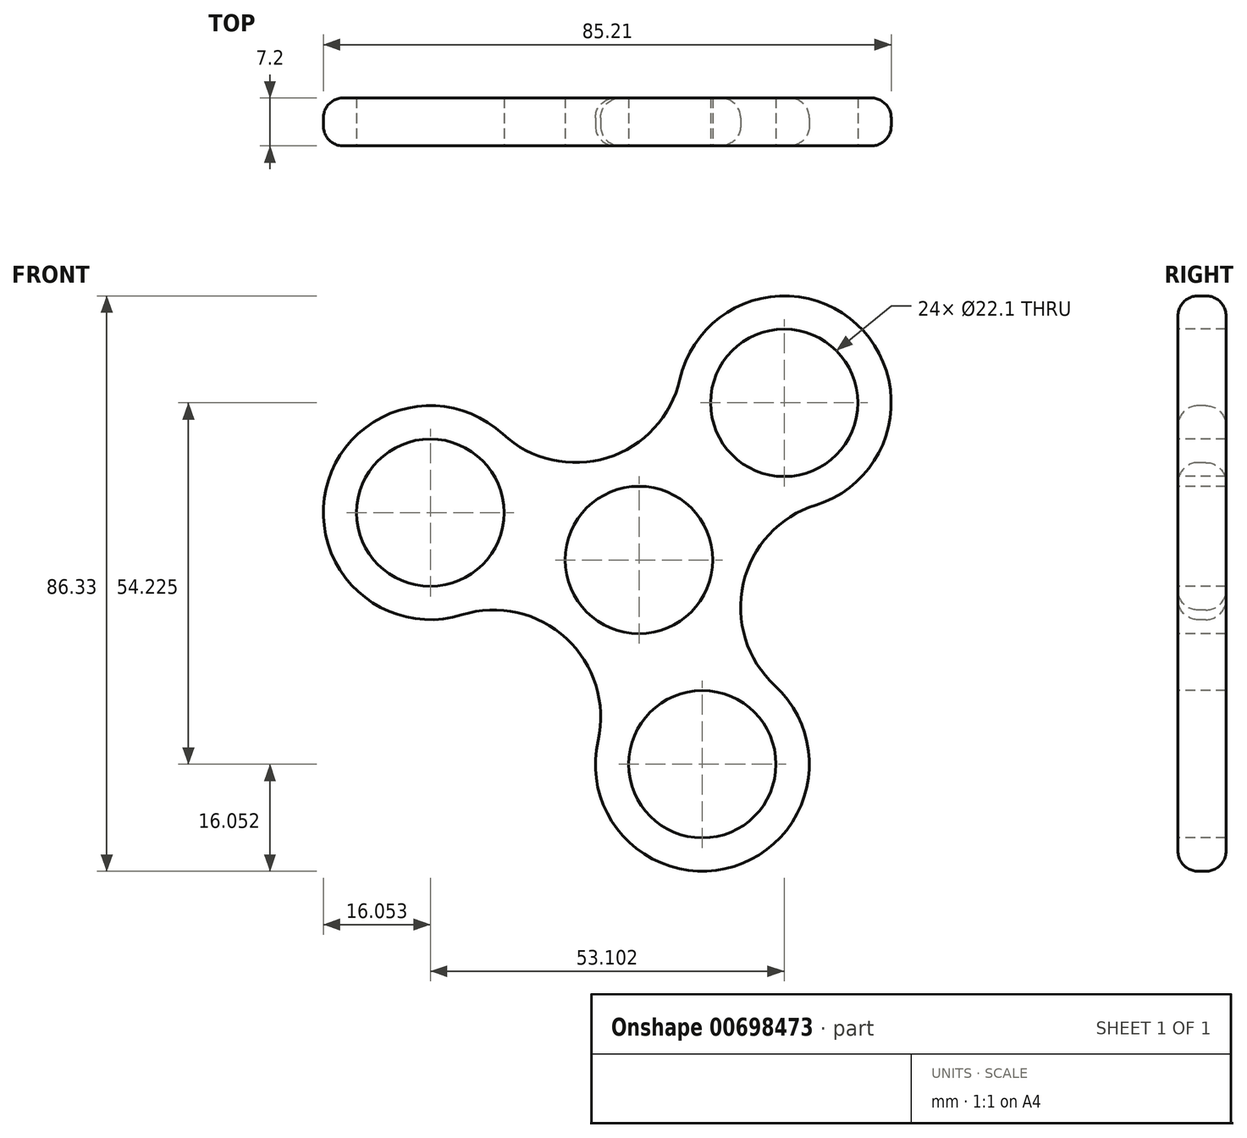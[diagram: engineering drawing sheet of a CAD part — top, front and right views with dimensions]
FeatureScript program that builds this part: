
annotation { "Feature Type Name" : "Feature", "Feature Type Description" : "" }
export const myFeature = defineFeature(function(context is Context, id is Id, definition is map)
    precondition{}
    {
        {
            var Q0;
            Q0=qCreatedBy(makeId("Front.planeOp"),FACE);
            var sketch = newSketch(context, id + "F0", { "sketchPlane" : qUnion([Q0])});
            skCircle(sketch, "E0", {"center": v(0, 0) * mm, "radius": 11.05 * mm});
            skCircle(sketch, "E1", {"center": v(-31.3, 7.1) * mm, "radius": 11.05 * mm});
            skCircle(sketch, "E2", {"center": v(21.8, 23.57) * mm, "radius": 11.05 * mm});
            skCircle(sketch, "E3", {"center": v(9.51, -30.66) * mm, "radius": 11.05 * mm});
            skLineSegment(sketch, "E4", {"start": v(21.8, 23.57) * mm, "end": v(0, 0) * mm});
            skLineSegment(sketch, "E5", {"start": v(0, 0) * mm, "end": v(-31.3, 7.1) * mm});
            skLineSegment(sketch, "E6", {"start": v(0, 0) * mm, "end": v(9.51, -30.66) * mm});
            skLineSegment(sketch, "E7", {"start": v(21.8, 23.57) * mm, "end": v(-31.3, 7.1) * mm, "construction": true});
            skLineSegment(sketch, "E8", {"start": v(-31.3, 7.1) * mm, "end": v(9.51, -30.66) * mm, "construction": true});
            skLineSegment(sketch, "E9", {"start": v(9.51, -30.66) * mm, "end": v(21.8, 23.57) * mm, "construction": true});
            skCircle(sketch, "E10.0", {"center": v(-31.3, 7.1) * mm, "radius": 16.05 * mm});
            skCircle(sketch, "E11.0", {"center": v(21.8, 23.57) * mm, "radius": 16.05 * mm});
            skCircle(sketch, "E12.0", {"center": v(9.51, -30.66) * mm, "radius": 16.05 * mm});
            skCircle(sketch, "E13.0", {"center": v(0, 0) * mm, "radius": 16.05 * mm});
            skLineSegment(sketch, "E14", {"start": v(0, 0) * mm, "end": v(-26.55, -8.24) * mm, "construction": true});
            skLineSegment(sketch, "E15", {"start": v(0, 0) * mm, "end": v(-6.14, -27.11) * mm, "construction": true});
            skArc(sketch, "E16", {"start": v(-6.14, -27.11) * mm, "mid": v(-10.9, -11.78) * mm, "end": v(-26.55, -8.24) * mm});
            skArc(sketch, "E17.1.0", {"start": v(26.55, 8.24) * mm, "mid": v(15.65, -3.55) * mm, "end": v(20.4, -18.88) * mm});
            skArc(sketch, "E17.2.0", {"start": v(-20.4, 18.88) * mm, "mid": v(-4.76, 15.33) * mm, "end": v(6.14, 27.11) * mm});
            skSolve(sketch);
        }
        {
            var Q0;
            Q0=makeQuery(id+"F0.imprint","IMPRINT",FACE,{"disambiguationData":[TD([[makeQuery(id+"F0.imprint","IMPRINT",EDGE,{"derivedFrom":sQuery(id+"F0.wireOp",EDGE,"E1")}),-1.0]])]});
            var Q1;
            {var subQ0=sQuery(id+"F0.wireOp",EDGE,"E17.2.0");var subQ1=sQuery(id+"F0.wireOp",EDGE,"E10.0");var subQ2=makeQuery(id+"F0.imprint","INTERSECT",VERTEX,{"derivedFrom":[subQ1,subQ0]});Q1=makeQuery(id+"F0.imprint","IMPRINT",FACE,{"disambiguationData":[TD([[makeQuery(id+"F0.imprint","IMPRINT",EDGE,{"disambiguationData":[TD([[subQ2,-1.0]])],"derivedFrom":subQ0}),-1.0]])]});}
            var Q2;
            {var subQ0=sQuery(id+"F0.wireOp",EDGE,"E17.2.0");var subQ1=sQuery(id+"F0.wireOp",EDGE,"E11.0");var subQ2=makeQuery(id+"F0.imprint","INTERSECT",VERTEX,{"derivedFrom":[subQ1,subQ0]});Q2=makeQuery(id+"F0.imprint","IMPRINT",FACE,{"disambiguationData":[TD([[makeQuery(id+"F0.imprint","IMPRINT",EDGE,{"disambiguationData":[TD([[subQ2,1.0]])],"derivedFrom":subQ0}),-1.0]])]});}
            var Q3;
            {var subQ0=sQuery(id+"F0.wireOp",EDGE,"E5");var subQ1=sQuery(id+"F0.wireOp",EDGE,"E0");var subQ2=makeQuery(id+"F0.imprint","INTERSECT",VERTEX,{"derivedFrom":[subQ1,subQ0]});Q3=makeQuery(id+"F0.imprint","IMPRINT",FACE,{"disambiguationData":[TD([[makeQuery(id+"F0.imprint","IMPRINT",EDGE,{"disambiguationData":[TD([[subQ2,1.0]])],"derivedFrom":subQ1}),-1.0]])]});}
            var Q4;
            Q4=makeQuery(id+"F0.imprint","IMPRINT",FACE,{"disambiguationData":[TD([[makeQuery(id+"F0.imprint","IMPRINT",EDGE,{"derivedFrom":sQuery(id+"F0.wireOp",EDGE,"E2")}),-1.0]])]});
            var Q5;
            {var subQ0=sQuery(id+"F0.wireOp",EDGE,"E17.1.0");var subQ1=sQuery(id+"F0.wireOp",EDGE,"E11.0");var subQ2=makeQuery(id+"F0.imprint","INTERSECT",VERTEX,{"derivedFrom":[subQ1,subQ0]});Q5=makeQuery(id+"F0.imprint","IMPRINT",FACE,{"disambiguationData":[TD([[makeQuery(id+"F0.imprint","IMPRINT",EDGE,{"disambiguationData":[TD([[subQ2,-1.0]])],"derivedFrom":subQ0}),-1.0]])]});}
            var Q6;
            {var subQ0=sQuery(id+"F0.wireOp",EDGE,"E17.1.0");var subQ1=sQuery(id+"F0.wireOp",EDGE,"E12.0");var subQ2=makeQuery(id+"F0.imprint","INTERSECT",VERTEX,{"derivedFrom":[subQ1,subQ0]});Q6=makeQuery(id+"F0.imprint","IMPRINT",FACE,{"disambiguationData":[TD([[makeQuery(id+"F0.imprint","IMPRINT",EDGE,{"disambiguationData":[TD([[subQ2,1.0]])],"derivedFrom":subQ0}),-1.0]])]});}
            var Q7;
            {var subQ4=sQuery(id+"F0.wireOp",EDGE,"E0");var subQ6=sQuery(id+"F0.wireOp",EDGE,"E4");var subQ7=makeQuery(id+"F0.imprint","INTERSECT",VERTEX,{"derivedFrom":[subQ4,subQ6]});Q7=makeQuery(id+"F0.imprint","IMPRINT",FACE,{"disambiguationData":[TD([[makeQuery(id+"F0.imprint","IMPRINT",EDGE,{"disambiguationData":[TD([[subQ7,1.0]])],"derivedFrom":subQ4}),-1.0]])]});}
            var Q8;
            {var subQ2=sQuery(id+"F0.wireOp",EDGE,"E5");var subQ4=sQuery(id+"F0.wireOp",EDGE,"E0");var subQ5=makeQuery(id+"F0.imprint","INTERSECT",VERTEX,{"derivedFrom":[subQ4,subQ2]});Q8=makeQuery(id+"F0.imprint","IMPRINT",FACE,{"disambiguationData":[TD([[makeQuery(id+"F0.imprint","IMPRINT",EDGE,{"disambiguationData":[TD([[subQ5,-1.0]])],"derivedFrom":subQ4}),-1.0]])]});}
            var Q9;
            {var subQ0=sQuery(id+"F0.wireOp",EDGE,"E16");var subQ3=sQuery(id+"F0.wireOp",EDGE,"E13.0");var subQ5=makeQuery(id+"F0.imprint","INTERSECT",VERTEX,{"derivedFrom":[subQ3,subQ0]});Q9=makeQuery(id+"F0.imprint","IMPRINT",FACE,{"disambiguationData":[TD([[makeQuery(id+"F0.imprint","IMPRINT",EDGE,{"disambiguationData":[TD([[subQ5,-1.0]])],"derivedFrom":subQ0}),-1.0]])]});}
            var Q10;
            {var subQ0=sQuery(id+"F0.wireOp",EDGE,"E16");var subQ3=sQuery(id+"F0.wireOp",EDGE,"E13.0");var subQ5=makeQuery(id+"F0.imprint","INTERSECT",VERTEX,{"derivedFrom":[subQ3,subQ0]});Q10=makeQuery(id+"F0.imprint","IMPRINT",FACE,{"disambiguationData":[TD([[makeQuery(id+"F0.imprint","IMPRINT",EDGE,{"disambiguationData":[TD([[subQ5,1.0]])],"derivedFrom":subQ0}),-1.0]])]});}
            var Q11;
            Q11=makeQuery(id+"F0.imprint","IMPRINT",FACE,{"disambiguationData":[TD([[makeQuery(id+"F0.imprint","IMPRINT",EDGE,{"derivedFrom":sQuery(id+"F0.wireOp",EDGE,"E3")}),-1.0]])]});
            extrude(context, id + "F1", {"entities" : qUnion([Q0, Q1, Q2, Q3, Q4, Q5, Q6, Q7, Q8, Q9, Q10, Q11]), "oppositeDirection" : true, "depth" : 7.2 * mm, "offsetDistance" : 25 * mm});
        }
        {
            var Q0;
            Q0=makeQuery(id+"F1.opExtrude","CAP_EDGE",EDGE,{"disambiguationData":[OSD([sQuery(id+"F0.wireOp",EDGE,"E17.2.0")])],"isStart":true});
            var Q1;
            Q1=makeQuery(id+"F1.opExtrude","CAP_EDGE",EDGE,{"disambiguationData":[OSD([sQuery(id+"F0.wireOp",EDGE,"E16")])],"isStart":false});
            fillet(context, id + "F2", {"entities" : qUnion([Q0, Q1]), "radius" : 3 * mm, "tangentPropagation" : true, "allowEdgeOverflow" : false});
        }
    });
